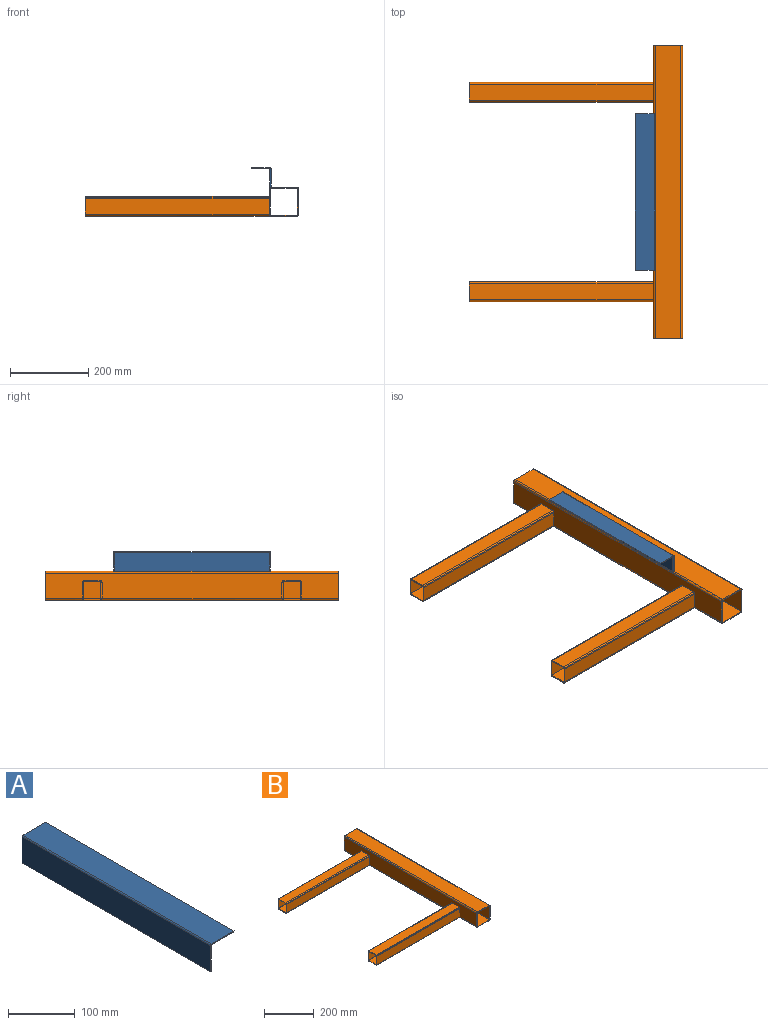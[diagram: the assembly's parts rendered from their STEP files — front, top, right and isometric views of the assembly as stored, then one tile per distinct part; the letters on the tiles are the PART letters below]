
ASSEMBLY  parts=2 mates=1
PART A: 11 faces, bbox 50x400x50 mm
  f0: plane 394x47mm, normal (0,0,-1), area 18518mm2, adj f1,f5,f8,f10
  f1: plane 400x3mm, normal (1,0,0), area 1196.1mm2, adj f0,f2,f8,f10
  f2: plane 400x48mm, normal (0,0,1), area 19200mm2, adj f1,f6,f8,f10
  f3: plane 400x48mm, normal (-1,0,0), area 19200mm2, adj f4,f6,f7,f9
  f4: plane 400x3mm, normal (0,0,-1), area 1196.1mm2, adj f3,f5,f7,f9
  f5: plane 394x47mm, normal (1,0,0), area 18518mm2, adj f0,f4,f7,f9
  f6: cylinder r=2mm len=400mm, axis (0,-1,0), area 1256.6mm2, adj f2,f3,f7,f8,f9,f10
  f7: cylinder r=3mm len=49.41mm, axis (0,0,1), area 226.2mm2, adj f3,f4,f5,f6,f8
  f8: cylinder r=3mm len=49.41mm, axis (1,0,0), area 226.2mm2, adj f0,f1,f2,f6,f7
  f9: cylinder r=3mm len=49.41mm, axis (0,0,-1), area 226.2mm2, adj f3,f4,f5,f6,f10
  f10: cylinder r=3mm len=49.41mm, axis (-1,0,0), area 226.2mm2, adj f0,f1,f2,f6,f9
PART B: 42 faces, bbox 545x750x75 mm
  f0: plane 750x65mm, normal (-1,0,0), area 44171.6mm2, adj f8,f9,f11,f12,f17,f21,f22,f27
  f1: plane 750x65mm, normal (0,0,-1), area 48750mm2, adj f8,f9,f30,f33
  f2: plane 750x65mm, normal (1,0,0), area 48750mm2, adj f8,f9,f30,f31
  f3: plane 750x65mm, normal (0,0,1), area 48750mm2, adj f8,f9,f31,f32
  f4: plane 750x69mm, normal (-1,0,0), area 51750mm2, adj f5,f7,f8,f9
  f5: plane 750x69mm, normal (0,0,1), area 51750mm2, adj f4,f6,f8,f9
  f6: plane 750x69mm, normal (1,0,0), area 51750mm2, adj f5,f7,f8,f9
  f7: plane 750x69mm, normal (0,0,-1), area 51750mm2, adj f4,f6,f8,f9
  f8: plane 75x75mm, normal (0,-1,0), area 842.5mm2, adj f0,f1,f2,f3,f4,f5,f6,f7
  f9: plane 75x75mm, normal (0,1,0), area 842.5mm2, adj f0,f1,f2,f3,f4,f5,f6,f7
  f10: plane 472x40mm, normal (0,0,-1), area 18880mm2, adj f18,f33,f38,f41
  f11: plane 470x40mm, normal (0,-1,0), area 18800mm2, adj f0,f18,f38,f39
  f12: plane 470x40mm, normal (0,0,1), area 18800mm2, adj f0,f18,f39,f40
  f13: plane 470x44mm, normal (0,-1,0), area 20680mm2, adj f14,f16,f18,f19
  f14: plane 470x44mm, normal (0,0,-1), area 20680mm2, adj f13,f15,f18,f19
  f15: plane 470x44mm, normal (0,1,0), area 20680mm2, adj f14,f16,f18,f19
  f16: plane 470x44mm, normal (0,0,1), area 20680mm2, adj f13,f15,f18,f19
  f17: plane 470x40mm, normal (0,1,0), area 18800mm2, adj f0,f18,f40,f41
  f18: plane 50x50mm, normal (-1,0,0), area 542.5mm2, adj f10,f11,f12,f13,f14,f15,f16,f17
  f19: plane 44x44mm, normal (-1,0,0), area 1936mm2, adj f13,f14,f15,f16
  f20: plane 472x40mm, normal (0,0,-1), area 18880mm2, adj f28,f33,f34,f37
  f21: plane 470x40mm, normal (0,-1,0), area 18800mm2, adj f0,f28,f34,f35
  f22: plane 470x40mm, normal (0,0,1), area 18800mm2, adj f0,f28,f35,f36
  f23: plane 470x44mm, normal (0,-1,0), area 20680mm2, adj f24,f26,f28,f29
  f24: plane 470x44mm, normal (0,0,-1), area 20680mm2, adj f23,f25,f28,f29
  f25: plane 470x44mm, normal (0,1,0), area 20680mm2, adj f24,f26,f28,f29
  f26: plane 470x44mm, normal (0,0,1), area 20680mm2, adj f23,f25,f28,f29
  f27: plane 470x40mm, normal (0,1,0), area 18800mm2, adj f0,f28,f36,f37
  f28: plane 50x50mm, normal (-1,0,0), area 542.5mm2, adj f20,f21,f22,f23,f24,f25,f26,f27
  f29: plane 44x44mm, normal (-1,0,0), area 1936mm2, adj f23,f24,f25,f26
  f30: cylinder r=5mm len=750mm, axis (0,-1,0), area 5890.5mm2, adj f1,f2,f8,f9
  f31: cylinder r=5mm len=750mm, axis (0,1,0), area 5890.5mm2, adj f2,f3,f8,f9
  f32: cylinder r=5mm len=750mm, axis (0,-1,0), area 5890.5mm2, adj f0,f3,f8,f9
  f33: cylinder r=5mm len=750mm, axis (0,1,0), area 5454.6mm2, adj f0,f1,f8,f9,f10,f20,f34,f37
  f34: cylinder r=5mm len=472mm, axis (-1,0,0), area 3697.9mm2, adj f0,f20,f21,f28,f33
  f35: cylinder r=5mm len=470mm, axis (1,0,0), area 3691.4mm2, adj f0,f21,f22,f28
  f36: cylinder r=5mm len=470mm, axis (-1,0,0), area 3691.4mm2, adj f0,f22,f27,f28
  f37: cylinder r=5mm len=472mm, axis (1,0,0), area 3697.9mm2, adj f0,f20,f27,f28,f33
  f38: cylinder r=5mm len=472mm, axis (-1,0,0), area 3697.9mm2, adj f0,f10,f11,f18,f33
  f39: cylinder r=5mm len=470mm, axis (1,0,0), area 3691.4mm2, adj f0,f11,f12,f18
  f40: cylinder r=5mm len=470mm, axis (-1,0,0), area 3691.4mm2, adj f0,f12,f17,f18
  f41: cylinder r=5mm len=472mm, axis (1,0,0), area 3697.9mm2, adj f0,f10,f17,f18,f33
PLACE A rot(axis=(0,1,0),90deg) t=(62.2,445.52,-55.92)mm
PLACE B t=(120.2,620.52,-118.42)mm
MATE planar B.f3 <-> A.f1  axis (0,0,1) through (120.2,245.52,-80.92)mm
